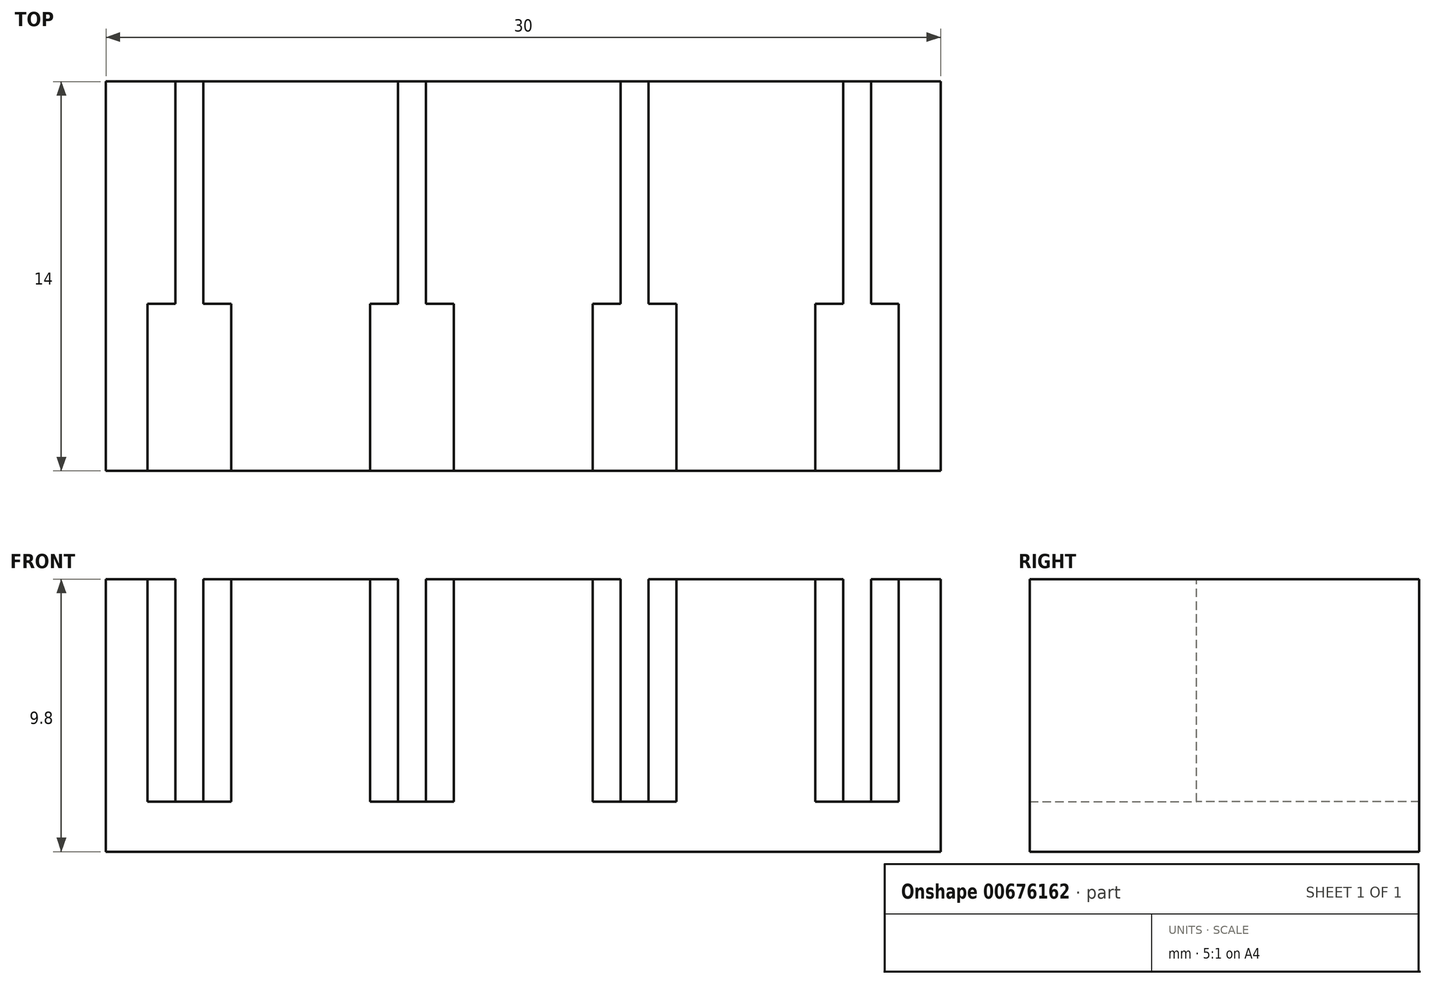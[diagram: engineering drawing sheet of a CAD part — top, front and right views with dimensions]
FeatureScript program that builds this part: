
annotation { "Feature Type Name" : "Feature", "Feature Type Description" : "" }
export const myFeature = defineFeature(function(context is Context, id is Id, definition is map)
    precondition{}
    {
        {
            var Q0;
            Q0=qCreatedBy(makeId("Top.planeOp"),FACE);
            var sketch = newSketch(context, id + "F0", { "sketchPlane" : qUnion([Q0])});
            skLineSegment(sketch, "E0.bottom", {"start": v(-15.47, 8.15) * mm, "end": v(14.53, 8.15) * mm});
            skLineSegment(sketch, "E0.top", {"start": v(-15.47, -5.85) * mm, "end": v(14.53, -5.85) * mm});
            skLineSegment(sketch, "E0.left", {"start": v(-15.47, 8.15) * mm, "end": v(-15.47, -5.85) * mm});
            skLineSegment(sketch, "E0.right", {"start": v(14.53, 8.15) * mm, "end": v(14.53, -5.85) * mm});
            skSolve(sketch);
        }
        {
            var Q0;
            Q0=makeQuery(id+"F0.imprint","IMPRINT",FACE,{"disambiguationData":[TD([[makeQuery(id+"F0.imprint","IMPRINT",EDGE,{"derivedFrom":sQuery(id+"F0.wireOp",EDGE,"E0.bottom")}),-1.0]])]});
            extrude(context, id + "F1", {"entities" : qUnion([Q0]), "depth" : 9.8 * mm, "offsetDistance" : 25 * mm});
        }
        {
            var Q0;
            Q0=makeQuery(id+"F1.opExtrude","CAP_FACE",FACE,{"disambiguationData":[OSD([sQuery(id+"F0.wireOp",EDGE,"E0.bottom"),sQuery(id+"F0.wireOp",EDGE,"E0.top"),sQuery(id+"F0.wireOp",EDGE,"E0.left"),sQuery(id+"F0.wireOp",EDGE,"E0.right")])],"isStart":false});
            var sketch = newSketch(context, id + "F2", { "sketchPlane" : qUnion([Q0])});
            skLineSegment(sketch, "E1.bottom", {"start": v(-12.97, 8.15) * mm, "end": v(-11.97, 8.15) * mm});
            skLineSegment(sketch, "E1.top", {"start": v(-12.97, -5.85) * mm, "end": v(-11.97, -5.85) * mm});
            skLineSegment(sketch, "E1.left", {"start": v(-12.97, 8.15) * mm, "end": v(-12.97, -5.85) * mm});
            skLineSegment(sketch, "E1.right", {"start": v(-11.97, 8.15) * mm, "end": v(-11.97, -5.85) * mm});
            skLineSegment(sketch, "E2.bottom", {"start": v(-4.97, 8.15) * mm, "end": v(-3.97, 8.15) * mm});
            skLineSegment(sketch, "E2.top", {"start": v(-4.97, -5.85) * mm, "end": v(-3.97, -5.85) * mm});
            skLineSegment(sketch, "E2.left", {"start": v(-4.97, 8.15) * mm, "end": v(-4.97, -5.85) * mm});
            skLineSegment(sketch, "E2.right", {"start": v(-3.97, 8.15) * mm, "end": v(-3.97, -5.85) * mm});
            skLineSegment(sketch, "E3.bottom", {"start": v(3.03, 8.15) * mm, "end": v(4.03, 8.15) * mm});
            skLineSegment(sketch, "E3.top", {"start": v(3.03, -5.85) * mm, "end": v(4.03, -5.85) * mm});
            skLineSegment(sketch, "E3.left", {"start": v(3.03, 8.15) * mm, "end": v(3.03, -5.85) * mm});
            skLineSegment(sketch, "E3.right", {"start": v(4.03, 8.15) * mm, "end": v(4.03, -5.85) * mm});
            skLineSegment(sketch, "E4.bottom", {"start": v(11.03, 8.15) * mm, "end": v(12.03, 8.15) * mm});
            skLineSegment(sketch, "E4.top", {"start": v(11.03, -5.85) * mm, "end": v(12.03, -5.85) * mm});
            skLineSegment(sketch, "E4.left", {"start": v(11.03, 8.15) * mm, "end": v(11.03, -5.85) * mm});
            skLineSegment(sketch, "E4.right", {"start": v(12.03, 8.15) * mm, "end": v(12.03, -5.85) * mm});
            skSolve(sketch);
        }
        {
            var Q0;
            Q0=makeQuery(id+"F1.opExtrude","CAP_FACE",FACE,{"disambiguationData":[OSD([sQuery(id+"F0.wireOp",EDGE,"E0.bottom"),sQuery(id+"F0.wireOp",EDGE,"E0.top"),sQuery(id+"F0.wireOp",EDGE,"E0.left"),sQuery(id+"F0.wireOp",EDGE,"E0.right")])],"isStart":false});
            var sketch = newSketch(context, id + "F3", { "sketchPlane" : qUnion([Q0])});
            skLineSegment(sketch, "E5.bottom", {"start": v(-13.97, -5.85) * mm, "end": v(-10.97, -5.85) * mm});
            skLineSegment(sketch, "E5.top", {"start": v(-13.97, 0.15) * mm, "end": v(-10.97, 0.15) * mm});
            skLineSegment(sketch, "E5.left", {"start": v(-13.97, -5.85) * mm, "end": v(-13.97, 0.15) * mm});
            skLineSegment(sketch, "E5.right", {"start": v(-10.97, -5.85) * mm, "end": v(-10.97, 0.15) * mm});
            skLineSegment(sketch, "E6.bottom", {"start": v(-5.97, -5.85) * mm, "end": v(-2.97, -5.85) * mm});
            skLineSegment(sketch, "E6.top", {"start": v(-5.97, 0.15) * mm, "end": v(-2.97, 0.15) * mm});
            skLineSegment(sketch, "E6.left", {"start": v(-5.97, -5.85) * mm, "end": v(-5.97, 0.15) * mm});
            skLineSegment(sketch, "E6.right", {"start": v(-2.97, -5.85) * mm, "end": v(-2.97, 0.15) * mm});
            skLineSegment(sketch, "E7.bottom", {"start": v(2.03, -5.85) * mm, "end": v(5.03, -5.85) * mm});
            skLineSegment(sketch, "E7.top", {"start": v(2.03, 0.15) * mm, "end": v(5.03, 0.15) * mm});
            skLineSegment(sketch, "E7.left", {"start": v(2.03, -5.85) * mm, "end": v(2.03, 0.15) * mm});
            skLineSegment(sketch, "E7.right", {"start": v(5.03, -5.85) * mm, "end": v(5.03, 0.15) * mm});
            skLineSegment(sketch, "E8.bottom", {"start": v(10.03, -5.85) * mm, "end": v(13.03, -5.85) * mm});
            skLineSegment(sketch, "E8.top", {"start": v(10.03, 0.15) * mm, "end": v(13.03, 0.15) * mm});
            skLineSegment(sketch, "E8.left", {"start": v(10.03, -5.85) * mm, "end": v(10.03, 0.15) * mm});
            skLineSegment(sketch, "E8.right", {"start": v(13.03, -5.85) * mm, "end": v(13.03, 0.15) * mm});
            skSolve(sketch);
        }
        {
            var Q0;
            Q0=makeQuery(id+"F2.imprint","IMPRINT",FACE,{"disambiguationData":[TD([[makeQuery(id+"F2.imprint","IMPRINT",EDGE,{"derivedFrom":sQuery(id+"F2.wireOp",EDGE,"E1.bottom")}),-1.0]])]});
            var Q1;
            Q1=makeQuery(id+"F2.imprint","IMPRINT",FACE,{"disambiguationData":[TD([[makeQuery(id+"F2.imprint","IMPRINT",EDGE,{"derivedFrom":sQuery(id+"F2.wireOp",EDGE,"E2.bottom")}),-1.0]])]});
            var Q2;
            Q2=makeQuery(id+"F2.imprint","IMPRINT",FACE,{"disambiguationData":[TD([[makeQuery(id+"F2.imprint","IMPRINT",EDGE,{"derivedFrom":sQuery(id+"F2.wireOp",EDGE,"E3.bottom")}),-1.0]])]});
            var Q3;
            Q3=makeQuery(id+"F2.imprint","IMPRINT",FACE,{"disambiguationData":[TD([[makeQuery(id+"F2.imprint","IMPRINT",EDGE,{"derivedFrom":sQuery(id+"F2.wireOp",EDGE,"E4.bottom")}),-1.0]])]});
            extrude(context, id + "F4", {"entities" : qUnion([Q0, Q1, Q2, Q3]), "operationType" : NewBodyOperationType.REMOVE, "oppositeDirection" : true, "depth" : 8 * mm, "offsetDistance" : 25 * mm});
        }
        {
            var Q0;
            Q0 = qSketchRegion(id + "F3", true);
            extrude(context, id + "F5", {"entities" : qUnion([Q0]), "operationType" : NewBodyOperationType.REMOVE, "oppositeDirection" : true, "depth" : 8 * mm, "offsetDistance" : 25 * mm});
        }
    });
